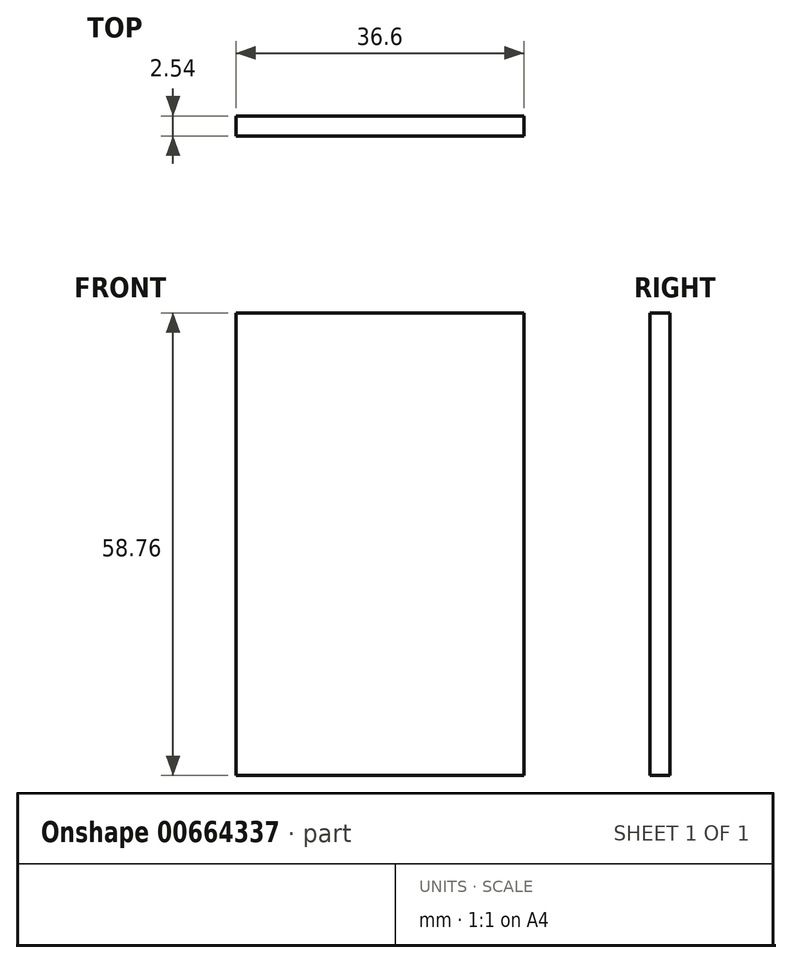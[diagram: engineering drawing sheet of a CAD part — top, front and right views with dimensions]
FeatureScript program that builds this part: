
annotation { "Feature Type Name" : "Feature", "Feature Type Description" : "" }
export const myFeature = defineFeature(function(context is Context, id is Id, definition is map)
    precondition{}
    {
        {
            var Q0;
            Q0=qCreatedBy(makeId("Front.planeOp"),FACE);
            var sketch = newSketch(context, id + "F0", { "sketchPlane" : qUnion([Q0])});
            skLineSegment(sketch, "E0.bottom", {"start": v(18.3, 29.38) * mm, "end": v(-18.3, 29.38) * mm});
            skLineSegment(sketch, "E0.top", {"start": v(18.3, -29.38) * mm, "end": v(-18.3, -29.38) * mm});
            skLineSegment(sketch, "E0.left", {"start": v(18.3, 29.38) * mm, "end": v(18.3, -29.38) * mm});
            skLineSegment(sketch, "E0.right", {"start": v(-18.3, 29.38) * mm, "end": v(-18.3, -29.38) * mm});
            skPoint(sketch, "E0.middle", {"position": v(0, 0) * mm});
            skSolve(sketch);
        }
        {
            var Q0;
            Q0 = qSketchRegion(id + "F0", true);
            extrude(context, id + "F1", {"entities" : qUnion([Q0]), "depth" : 2.54 * mm, "offsetDistance" : 25.4 * mm});
        }
    });
